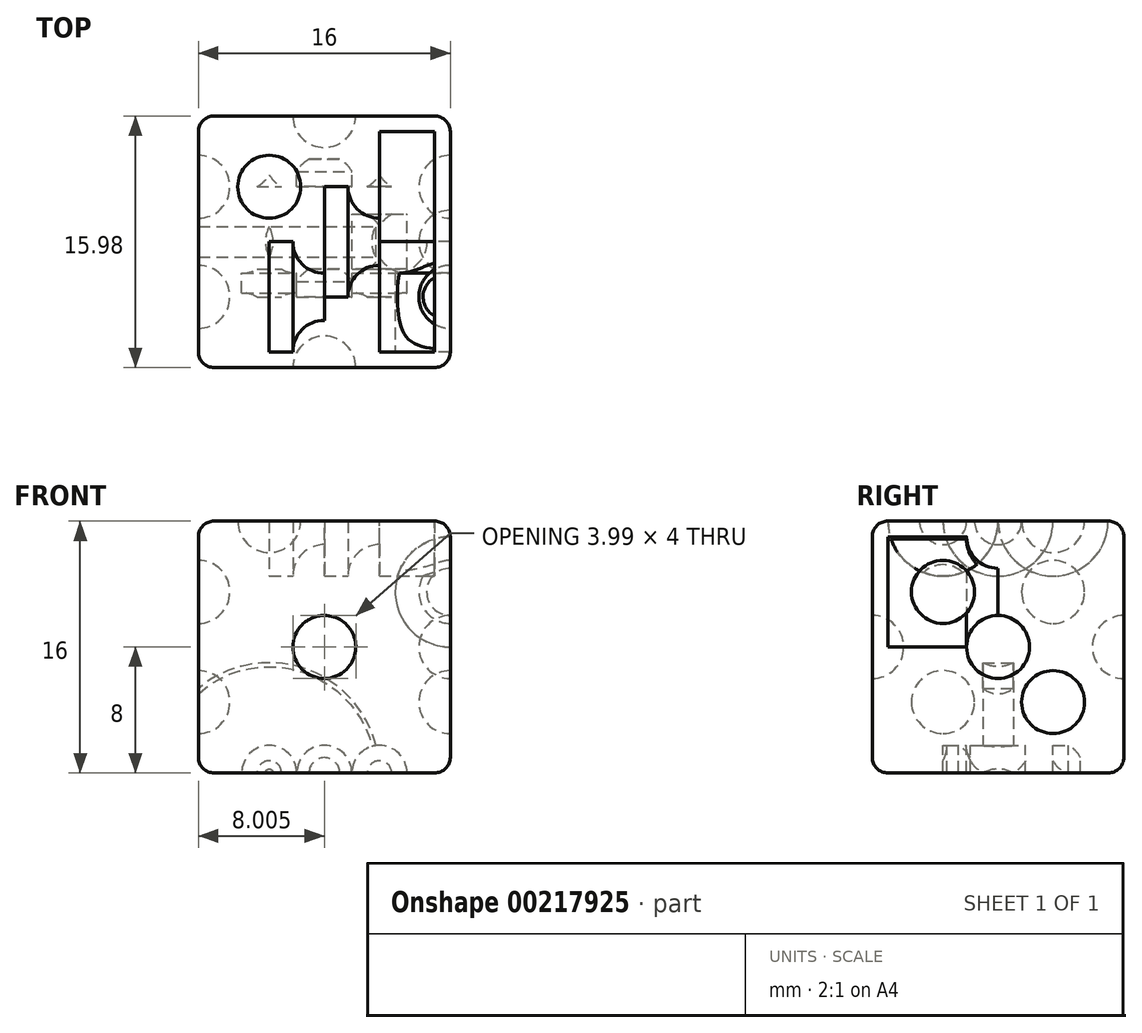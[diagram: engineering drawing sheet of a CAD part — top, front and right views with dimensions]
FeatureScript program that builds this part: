
annotation { "Feature Type Name" : "Feature", "Feature Type Description" : "" }
export const myFeature = defineFeature(function(context is Context, id is Id, definition is map)
    precondition{}
    {
        {
            assignVariable(context, id + "F0", {"name" : "SIZE", "anyValue" : 16});
        }
        {
            var Q0;
            Q0=qCreatedBy(makeId("Top.planeOp"),FACE);
            var sketch = newSketch(context, id + "F1", { "sketchPlane" : qUnion([Q0])});
            skLineSegment(sketch, "E0.bottom", {"start": v(0, 0) * mm, "end": v(16, 0) * mm});
            skLineSegment(sketch, "E0.top", {"start": v(0, -15.98) * mm, "end": v(16, -15.98) * mm});
            skLineSegment(sketch, "E0.left", {"start": v(0, 0) * mm, "end": v(0, -15.98) * mm});
            skLineSegment(sketch, "E0.right", {"start": v(16, 0) * mm, "end": v(16, -15.98) * mm});
            skSolve(sketch);
        }
        {
            var Q0;
            Q0=makeQuery(id+"F1.imprint","IMPRINT",FACE,{"disambiguationData":[TD([[makeQuery(id+"F1.imprint","IMPRINT",EDGE,{"derivedFrom":sQuery(id+"F1.wireOp",EDGE,"E0.bottom")}),-1.0]])]});
            extrude(context, id + "F2", {"entities" : qUnion([Q0]), "depth" : getVariable(context, 'SIZE') * mm});
        }
        {
            var Q0;
            Q0=makeQuery(id+"F2.opExtrude","CAP_EDGE",EDGE,{"disambiguationData":[OSD([sQuery(id+"F1.wireOp",EDGE,"E0.left")])],"isStart":false});
            var Q1;
            Q1=makeQuery(id+"F2.opExtrude","CAP_EDGE",EDGE,{"disambiguationData":[OSD([sQuery(id+"F1.wireOp",EDGE,"E0.top")])],"isStart":false});
            var Q2;
            Q2=makeQuery(id+"F2.opExtrude","CAP_EDGE",EDGE,{"disambiguationData":[OSD([sQuery(id+"F1.wireOp",EDGE,"E0.right")])],"isStart":false});
            var Q3;
            Q3=makeQuery(id+"F2.opExtrude","CAP_EDGE",EDGE,{"disambiguationData":[OSD([sQuery(id+"F1.wireOp",EDGE,"E0.bottom")])],"isStart":false});
            var Q4;
            Q4=makeQuery(id+"F2.opExtrude","SWEPT_EDGE",EDGE,{"disambiguationData":[OSD([sQuery(id+"F1.wireOp",EDGE,"E0.top"),sQuery(id+"F1.wireOp",EDGE,"E0.left")])]});
            var Q5;
            Q5=makeQuery(id+"F2.opExtrude","SWEPT_EDGE",EDGE,{"disambiguationData":[OSD([sQuery(id+"F1.wireOp",EDGE,"E0.bottom"),sQuery(id+"F1.wireOp",EDGE,"E0.left")])]});
            var Q6;
            Q6=makeQuery(id+"F2.opExtrude","SWEPT_EDGE",EDGE,{"disambiguationData":[OSD([sQuery(id+"F1.wireOp",EDGE,"E0.top"),sQuery(id+"F1.wireOp",EDGE,"E0.right")])]});
            var Q7;
            Q7=makeQuery(id+"F2.opExtrude","SWEPT_EDGE",EDGE,{"disambiguationData":[OSD([sQuery(id+"F1.wireOp",EDGE,"E0.bottom"),sQuery(id+"F1.wireOp",EDGE,"E0.right")])]});
            var Q8;
            Q8=makeQuery(id+"F2.opExtrude","CAP_EDGE",EDGE,{"disambiguationData":[OSD([sQuery(id+"F1.wireOp",EDGE,"E0.bottom")])],"isStart":true});
            var Q9;
            Q9=makeQuery(id+"F2.opExtrude","CAP_EDGE",EDGE,{"disambiguationData":[OSD([sQuery(id+"F1.wireOp",EDGE,"E0.left")])],"isStart":true});
            var Q10;
            Q10=makeQuery(id+"F2.opExtrude","CAP_EDGE",EDGE,{"disambiguationData":[OSD([sQuery(id+"F1.wireOp",EDGE,"E0.top")])],"isStart":true});
            var Q11;
            Q11=makeQuery(id+"F2.opExtrude","CAP_EDGE",EDGE,{"disambiguationData":[OSD([sQuery(id+"F1.wireOp",EDGE,"E0.right")])],"isStart":true});
            fillet(context, id + "F3", {"entities" : qUnion([Q0, Q1, Q2, Q3, Q4, Q5, Q6, Q7, Q8, Q9, Q10, Q11]), "radius" : 1 * mm, "tangentPropagation" : true, "allowEdgeOverflow" : false});
        }
        {
            var Q0;
            Q0=makeQuery(id+"F2.opExtrude","SWEPT_FACE",FACE,{"disambiguationData":[OSD([sQuery(id+"F1.wireOp",EDGE,"E0.top")])]});
            var sketch = newSketch(context, id + "F4", { "sketchPlane" : qUnion([Q0])});
            skCircle(sketch, "E1", {"center": v(8, 8) * mm, "radius": 2 * mm});
            skLineSegment(sketch, "E2", {"start": v(1, 15) * mm, "end": v(15, 1) * mm});
            skSolve(sketch);
        }
        {
            var Q0;
            {var subQ0=sQuery(id+"F4.wireOp",EDGE,"E2");var subQ1=sQuery(id+"F4.wireOp",EDGE,"E1");var subQ2=makeQuery(id+"F4.imprint","INTERSECT",VERTEX,{"disambiguationData":[OD(0.0)],"derivedFrom":[subQ1,subQ0]});Q0=makeQuery(id+"F4.imprint","IMPRINT",FACE,{"disambiguationData":[TD([[makeQuery(id+"F4.imprint","IMPRINT",EDGE,{"disambiguationData":[TD([[subQ2,1.0]])],"derivedFrom":subQ1}),1.0]])]});}
            var Q1;
            Q1=sQuery(id+"F4.wireOp",EDGE,"E1");
            var Q2;
            Q2=sQuery(id+"F4.wireOp",EDGE,"E2");
            revolve(context, id + "F5", {"operationType" : NewBodyOperationType.REMOVE, "entities" : qUnion([Q0]), "surfaceEntities" : qUnion([Q1]), "axis" : qUnion([Q2]), "revolveType" : RevolveType.FULL, "oppositeDirection" : true});
        }
        {
            var Q0;
            Q0=makeQuery(id+"F2.opExtrude","SWEPT_FACE",FACE,{"disambiguationData":[OSD([sQuery(id+"F1.wireOp",EDGE,"E0.bottom")])]});
            var sketch = newSketch(context, id + "F6", { "sketchPlane" : qUnion([Q0])});
            skLineSegment(sketch, "E3", {"start": v(-15, 15) * mm, "end": v(-1, 1) * mm});
            skCircle(sketch, "E4", {"center": v(-8, 8) * mm, "radius": 2 * mm});
            skSolve(sketch);
        }
        {
            var Q0;
            {var subQ0=sQuery(id+"F6.wireOp",EDGE,"E4");var subQ1=sQuery(id+"F6.wireOp",EDGE,"E3");var subQ2=makeQuery(id+"F6.imprint","INTERSECT",VERTEX,{"disambiguationData":[OD(0.0)],"derivedFrom":[subQ1,subQ0]});Q0=makeQuery(id+"F6.imprint","IMPRINT",FACE,{"disambiguationData":[TD([[makeQuery(id+"F6.imprint","IMPRINT",EDGE,{"disambiguationData":[TD([[subQ2,-1.0]])],"derivedFrom":subQ1}),1.0]])]});}
            var Q1;
            Q1=sQuery(id+"F6.wireOp",EDGE,"E3");
            revolve(context, id + "F7", {"operationType" : NewBodyOperationType.REMOVE, "entities" : qUnion([Q0]), "axis" : qUnion([Q1]), "revolveType" : RevolveType.FULL});
        }
        {
            var Q0;
            Q0=makeQuery(id+"F2.opExtrude","SWEPT_FACE",FACE,{"disambiguationData":[OSD([sQuery(id+"F1.wireOp",EDGE,"E0.left")])]});
            var sketch = newSketch(context, id + "F8", { "sketchPlane" : qUnion([Q0])});
            skCircle(sketch, "E5", {"center": v(4.5, 11.5) * mm, "radius": 2 * mm});
            skCircle(sketch, "E6", {"center": v(11.49, 4.5) * mm, "radius": 2 * mm});
            skLineSegment(sketch, "E7", {"start": v(8, 15) * mm, "end": v(8, 1) * mm});
            skLineSegment(sketch, "E8", {"start": v(1, 15) * mm, "end": v(1, 1) * mm});
            skLineSegment(sketch, "E9", {"start": v(1, 1) * mm, "end": v(8, 1) * mm});
            skLineSegment(sketch, "E10", {"start": v(1, 15) * mm, "end": v(8, 15) * mm});
            skLineSegment(sketch, "E11", {"start": v(4.5, 15) * mm, "end": v(4.5, 1) * mm});
            skLineSegment(sketch, "E12", {"start": v(8, 15) * mm, "end": v(14.98, 15) * mm});
            skLineSegment(sketch, "E13", {"start": v(14.98, 15) * mm, "end": v(14.98, 1) * mm});
            skLineSegment(sketch, "E14", {"start": v(14.98, 1) * mm, "end": v(8, 1) * mm});
            skLineSegment(sketch, "E15", {"start": v(11.49, 15) * mm, "end": v(11.49, 1) * mm});
            skLineSegment(sketch, "E16", {"start": v(1, 8) * mm, "end": v(14.98, 8) * mm});
            skLineSegment(sketch, "E17", {"start": v(1, 8) * mm, "end": v(1, 15) * mm});
            skLineSegment(sketch, "E18", {"start": v(1, 8) * mm, "end": v(1, 1) * mm});
            skLineSegment(sketch, "E19", {"start": v(14.98, 15) * mm, "end": v(14.98, 8) * mm});
            skLineSegment(sketch, "E20", {"start": v(14.98, 8) * mm, "end": v(14.98, 1) * mm});
            skLineSegment(sketch, "E21", {"start": v(1, 11.5) * mm, "end": v(14.98, 11.5) * mm});
            skLineSegment(sketch, "E22", {"start": v(1, 4.5) * mm, "end": v(14.98, 4.5) * mm});
            skSolve(sketch);
        }
        {
            var Q0;
            {var subQ0=sQuery(id+"F8.wireOp",EDGE,"E11");var subQ1=sQuery(id+"F8.wireOp",EDGE,"E5");var subQ2=makeQuery(id+"F8.imprint","INTERSECT",VERTEX,{"disambiguationData":[OD(0.0)],"derivedFrom":[subQ1,subQ0]});Q0=makeQuery(id+"F8.imprint","IMPRINT",FACE,{"disambiguationData":[TD([[makeQuery(id+"F8.imprint","IMPRINT",EDGE,{"disambiguationData":[TD([[subQ2,-1.0]])],"derivedFrom":subQ1}),1.0]])]});}
            var Q1;
            {var subQ0=sQuery(id+"F8.wireOp",EDGE,"E11");var subQ1=sQuery(id+"F8.wireOp",EDGE,"E5");var subQ2=makeQuery(id+"F8.imprint","INTERSECT",VERTEX,{"disambiguationData":[OD(0.0)],"derivedFrom":[subQ1,subQ0]});Q1=makeQuery(id+"F8.imprint","IMPRINT",FACE,{"disambiguationData":[TD([[makeQuery(id+"F8.imprint","IMPRINT",EDGE,{"disambiguationData":[TD([[subQ2,1.0]])],"derivedFrom":subQ1}),1.0]])]});}
            var Q2;
            Q2=sQuery(id+"F8.wireOp",EDGE,"E21");
            revolve(context, id + "F9", {"operationType" : NewBodyOperationType.REMOVE, "entities" : qUnion([Q0, Q1]), "axis" : qUnion([Q2]), "revolveType" : RevolveType.FULL, "oppositeDirection" : true});
        }
        {
            var Q0;
            {var subQ0=sQuery(id+"F8.wireOp",EDGE,"E22");var subQ1=sQuery(id+"F8.wireOp",EDGE,"E6");var subQ2=makeQuery(id+"F8.imprint","INTERSECT",VERTEX,{"disambiguationData":[OD(1.0)],"derivedFrom":[subQ1,subQ0]});Q0=makeQuery(id+"F8.imprint","IMPRINT",FACE,{"disambiguationData":[TD([[makeQuery(id+"F8.imprint","IMPRINT",EDGE,{"disambiguationData":[TD([[subQ2,-1.0]])],"derivedFrom":subQ1}),1.0]])]});}
            var Q1;
            {var subQ0=sQuery(id+"F8.wireOp",EDGE,"E22");var subQ1=sQuery(id+"F8.wireOp",EDGE,"E6");var subQ2=makeQuery(id+"F8.imprint","INTERSECT",VERTEX,{"disambiguationData":[OD(0.0)],"derivedFrom":[subQ1,subQ0]});Q1=makeQuery(id+"F8.imprint","IMPRINT",FACE,{"disambiguationData":[TD([[makeQuery(id+"F8.imprint","IMPRINT",EDGE,{"disambiguationData":[TD([[subQ2,1.0]])],"derivedFrom":subQ1}),1.0]])]});}
            var Q2;
            Q2=sQuery(id+"F8.wireOp",EDGE,"E22");
            revolve(context, id + "F10", {"operationType" : NewBodyOperationType.REMOVE, "entities" : qUnion([Q0, Q1]), "axis" : qUnion([Q2]), "revolveType" : RevolveType.FULL, "oppositeDirection" : true});
        }
        {
            var Q0;
            Q0=makeQuery(id+"F2.opExtrude","SWEPT_FACE",FACE,{"disambiguationData":[OSD([sQuery(id+"F1.wireOp",EDGE,"E0.right")])]});
            var sketch = newSketch(context, id + "F11", { "sketchPlane" : qUnion([Q0])});
            skLineSegment(sketch, "E23", {"start": v(-8, 15) * mm, "end": v(-8, 1) * mm});
            skLineSegment(sketch, "E24", {"start": v(-8, 1) * mm, "end": v(-14.98, 1) * mm});
            skLineSegment(sketch, "E25", {"start": v(-14.98, 1) * mm, "end": v(-14.98, 15) * mm});
            skLineSegment(sketch, "E26", {"start": v(-14.98, 15) * mm, "end": v(-8, 15) * mm});
            skLineSegment(sketch, "E27", {"start": v(-1, 15) * mm, "end": v(-1, 8) * mm});
            skLineSegment(sketch, "E28", {"start": v(-1, 8) * mm, "end": v(-1, 1) * mm});
            skLineSegment(sketch, "E29", {"start": v(-1, 1) * mm, "end": v(-8, 1) * mm});
            skLineSegment(sketch, "E30", {"start": v(-8, 8) * mm, "end": v(-14.98, 8) * mm});
            skLineSegment(sketch, "E31", {"start": v(-8, 8) * mm, "end": v(-1, 8) * mm});
            skLineSegment(sketch, "E32", {"start": v(-1, 15) * mm, "end": v(-8, 15) * mm});
            skLineSegment(sketch, "E33", {"start": v(-4.5, 15) * mm, "end": v(-4.5, 8) * mm});
            skLineSegment(sketch, "E34", {"start": v(-4.5, 8) * mm, "end": v(-4.5, 1) * mm});
            skLineSegment(sketch, "E35", {"start": v(-11.49, 15) * mm, "end": v(-11.49, 8) * mm});
            skLineSegment(sketch, "E36", {"start": v(-11.49, 8) * mm, "end": v(-11.49, 1) * mm});
            skLineSegment(sketch, "E37", {"start": v(-14.98, 8) * mm, "end": v(-14.98, 15) * mm});
            skLineSegment(sketch, "E38", {"start": v(-1, 11.5) * mm, "end": v(-14.98, 11.5) * mm});
            skLineSegment(sketch, "E39", {"start": v(-14.98, 8) * mm, "end": v(-14.98, 1) * mm});
            skLineSegment(sketch, "E40", {"start": v(-14.98, 4.5) * mm, "end": v(-1, 4.5) * mm});
            skCircle(sketch, "E41", {"center": v(-11.49, 11.5) * mm, "radius": 2 * mm});
            skCircle(sketch, "E42", {"center": v(-8, 8) * mm, "radius": 2 * mm});
            skCircle(sketch, "E43", {"center": v(-4.5, 4.5) * mm, "radius": 2 * mm});
            skSolve(sketch);
        }
        {
            var Q0;
            {var subQ0=sQuery(id+"F11.wireOp",EDGE,"E41");var subQ1=sQuery(id+"F11.wireOp",EDGE,"E35");var subQ2=makeQuery(id+"F11.imprint","INTERSECT",VERTEX,{"disambiguationData":[OD(0.0)],"derivedFrom":[subQ1,subQ0]});Q0=makeQuery(id+"F11.imprint","IMPRINT",FACE,{"disambiguationData":[TD([[makeQuery(id+"F11.imprint","IMPRINT",EDGE,{"disambiguationData":[TD([[subQ2,-1.0]])],"derivedFrom":subQ1}),-1.0]])]});}
            var Q1;
            {var subQ0=sQuery(id+"F11.wireOp",EDGE,"E41");var subQ1=sQuery(id+"F11.wireOp",EDGE,"E35");var subQ2=makeQuery(id+"F11.imprint","INTERSECT",VERTEX,{"disambiguationData":[OD(0.0)],"derivedFrom":[subQ1,subQ0]});Q1=makeQuery(id+"F11.imprint","IMPRINT",FACE,{"disambiguationData":[TD([[makeQuery(id+"F11.imprint","IMPRINT",EDGE,{"disambiguationData":[TD([[subQ2,-1.0]])],"derivedFrom":subQ1}),1.0]])]});}
            var Q2;
            Q2=sQuery(id+"F11.wireOp",EDGE,"E38");
            revolve(context, id + "F12", {"operationType" : NewBodyOperationType.REMOVE, "entities" : qUnion([Q0, Q1]), "axis" : qUnion([Q2]), "revolveType" : RevolveType.FULL, "oppositeDirection" : true});
        }
        {
            var Q0;
            {var subQ1=sQuery(id+"F11.wireOp",EDGE,"E23");var subQ3=sQuery(id+"F11.wireOp",EDGE,"E42");var subQ4=makeQuery(id+"F11.imprint","INTERSECT",VERTEX,{"disambiguationData":[OD(0.0)],"derivedFrom":[subQ1,subQ3]});Q0=makeQuery(id+"F11.imprint","IMPRINT",FACE,{"disambiguationData":[TD([[makeQuery(id+"F11.imprint","IMPRINT",EDGE,{"disambiguationData":[TD([[subQ4,-1.0]])],"derivedFrom":subQ3}),1.0]])]});}
            var Q1;
            {var subQ1=sQuery(id+"F11.wireOp",EDGE,"E23");var subQ3=sQuery(id+"F11.wireOp",EDGE,"E42");var subQ4=makeQuery(id+"F11.imprint","INTERSECT",VERTEX,{"disambiguationData":[OD(0.0)],"derivedFrom":[subQ1,subQ3]});Q1=makeQuery(id+"F11.imprint","IMPRINT",FACE,{"disambiguationData":[TD([[makeQuery(id+"F11.imprint","IMPRINT",EDGE,{"disambiguationData":[TD([[subQ4,1.0]])],"derivedFrom":subQ3}),1.0]])]});}
            var Q2;
            Q2=sQuery(id+"F11.wireOp",EDGE,"E31");
            revolve(context, id + "F13", {"operationType" : NewBodyOperationType.REMOVE, "entities" : qUnion([Q0, Q1]), "axis" : qUnion([Q2]), "revolveType" : RevolveType.FULL, "oppositeDirection" : true});
        }
        {
            var Q0;
            {var subQ0=sQuery(id+"F11.wireOp",EDGE,"E43");var subQ1=sQuery(id+"F11.wireOp",EDGE,"E34");var subQ2=makeQuery(id+"F11.imprint","INTERSECT",VERTEX,{"disambiguationData":[OD(0.0)],"derivedFrom":[subQ1,subQ0]});Q0=makeQuery(id+"F11.imprint","IMPRINT",FACE,{"disambiguationData":[TD([[makeQuery(id+"F11.imprint","IMPRINT",EDGE,{"disambiguationData":[TD([[subQ2,-1.0]])],"derivedFrom":subQ1}),-1.0]])]});}
            var Q1;
            {var subQ0=sQuery(id+"F11.wireOp",EDGE,"E43");var subQ1=sQuery(id+"F11.wireOp",EDGE,"E34");var subQ2=makeQuery(id+"F11.imprint","INTERSECT",VERTEX,{"disambiguationData":[OD(0.0)],"derivedFrom":[subQ1,subQ0]});Q1=makeQuery(id+"F11.imprint","IMPRINT",FACE,{"disambiguationData":[TD([[makeQuery(id+"F11.imprint","IMPRINT",EDGE,{"disambiguationData":[TD([[subQ2,-1.0]])],"derivedFrom":subQ1}),1.0]])]});}
            var Q2;
            Q2=sQuery(id+"F11.wireOp",EDGE,"E40");
            revolve(context, id + "F14", {"operationType" : NewBodyOperationType.REMOVE, "entities" : qUnion([Q0, Q1]), "axis" : qUnion([Q2]), "revolveType" : RevolveType.FULL});
        }
        {
            var Q0;
            Q0=makeQuery(id+"F2.opExtrude","CAP_FACE",FACE,{"disambiguationData":[OSD([sQuery(id+"F1.wireOp",EDGE,"E0.bottom"),sQuery(id+"F1.wireOp",EDGE,"E0.top"),sQuery(id+"F1.wireOp",EDGE,"E0.left"),sQuery(id+"F1.wireOp",EDGE,"E0.right")])],"isStart":false});
            var sketch = newSketch(context, id + "F15", { "sketchPlane" : qUnion([Q0])});
            skLineSegment(sketch, "E44", {"start": v(1, -14.98) * mm, "end": v(1, -1) * mm});
            skLineSegment(sketch, "E45", {"start": v(1, -1) * mm, "end": v(15, -1) * mm});
            skLineSegment(sketch, "E46", {"start": v(15, -1) * mm, "end": v(15, -14.98) * mm});
            skLineSegment(sketch, "E47", {"start": v(15, -14.98) * mm, "end": v(1, -14.98) * mm});
            skLineSegment(sketch, "E48", {"start": v(1, -8) * mm, "end": v(15, -8) * mm});
            skLineSegment(sketch, "E49", {"start": v(8, -1) * mm, "end": v(8, -14.98) * mm});
            skLineSegment(sketch, "E50", {"start": v(1, -14.98) * mm, "end": v(8, -14.98) * mm});
            skLineSegment(sketch, "E51", {"start": v(8, -14.98) * mm, "end": v(15, -14.98) * mm});
            skLineSegment(sketch, "E52", {"start": v(15, -14.98) * mm, "end": v(15, -8) * mm});
            skLineSegment(sketch, "E53", {"start": v(15, -8) * mm, "end": v(15, -1) * mm});
            skLineSegment(sketch, "E54", {"start": v(15, -1) * mm, "end": v(8, -1) * mm});
            skLineSegment(sketch, "E55", {"start": v(8, -1) * mm, "end": v(1, -1) * mm});
            skLineSegment(sketch, "E56", {"start": v(1, -1) * mm, "end": v(1, -8) * mm});
            skLineSegment(sketch, "E57", {"start": v(1, -8) * mm, "end": v(1, -14.98) * mm});
            skLineSegment(sketch, "E58", {"start": v(1, -11.49) * mm, "end": v(15, -11.49) * mm});
            skLineSegment(sketch, "E59", {"start": v(1, -4.5) * mm, "end": v(15, -4.5) * mm});
            skLineSegment(sketch, "E60", {"start": v(4.5, -1) * mm, "end": v(4.5, -14.98) * mm});
            skLineSegment(sketch, "E61", {"start": v(11.5, -1) * mm, "end": v(11.5, -14.98) * mm});
            skCircle(sketch, "E62", {"center": v(4.5, -4.5) * mm, "radius": 2 * mm});
            skCircle(sketch, "E63", {"center": v(4.5, -11.49) * mm, "radius": 2 * mm});
            skCircle(sketch, "E64", {"center": v(11.5, -11.49) * mm, "radius": 2 * mm});
            skCircle(sketch, "E65", {"center": v(11.5, -4.5) * mm, "radius": 2 * mm});
            skCircle(sketch, "E66", {"center": v(8, -8) * mm, "radius": 2 * mm});
            skSolve(sketch);
        }
        {
            var Q0;
            {var subQ0=sQuery(id+"F15.wireOp",EDGE,"E62");var subQ1=sQuery(id+"F15.wireOp",EDGE,"E59");var subQ2=makeQuery(id+"F15.imprint","INTERSECT",VERTEX,{"disambiguationData":[OD(0.0)],"derivedFrom":[subQ1,subQ0]});Q0=makeQuery(id+"F15.imprint","IMPRINT",FACE,{"disambiguationData":[TD([[makeQuery(id+"F15.imprint","IMPRINT",EDGE,{"disambiguationData":[TD([[subQ2,-1.0]])],"derivedFrom":subQ1}),1.0]])]});}
            var Q1;
            {var subQ0=sQuery(id+"F15.wireOp",EDGE,"E60");var subQ1=sQuery(id+"F15.wireOp",EDGE,"E59");var subQ2=makeQuery(id+"F15.imprint","INTERSECT",VERTEX,{"derivedFrom":[subQ1,subQ0]});Q1=makeQuery(id+"F15.imprint","IMPRINT",FACE,{"disambiguationData":[TD([[makeQuery(id+"F15.imprint","IMPRINT",EDGE,{"disambiguationData":[TD([[subQ2,-1.0]])],"derivedFrom":subQ1}),1.0]])]});}
            var Q2;
            {var subQ0=sQuery(id+"F15.wireOp",EDGE,"E65");var subQ1=sQuery(id+"F15.wireOp",EDGE,"E59");var subQ2=makeQuery(id+"F15.imprint","INTERSECT",VERTEX,{"disambiguationData":[OD(0.0)],"derivedFrom":[subQ1,subQ0]});Q2=makeQuery(id+"F15.imprint","IMPRINT",FACE,{"disambiguationData":[TD([[makeQuery(id+"F15.imprint","IMPRINT",EDGE,{"disambiguationData":[TD([[subQ2,-1.0]])],"derivedFrom":subQ1}),1.0]])]});}
            var Q3;
            {var subQ0=sQuery(id+"F15.wireOp",EDGE,"E61");var subQ1=sQuery(id+"F15.wireOp",EDGE,"E59");var subQ2=makeQuery(id+"F15.imprint","INTERSECT",VERTEX,{"derivedFrom":[subQ1,subQ0]});Q3=makeQuery(id+"F15.imprint","IMPRINT",FACE,{"disambiguationData":[TD([[makeQuery(id+"F15.imprint","IMPRINT",EDGE,{"disambiguationData":[TD([[subQ2,-1.0]])],"derivedFrom":subQ1}),1.0]])]});}
            var Q4;
            Q4=sQuery(id+"F15.wireOp",EDGE,"E59");
            revolve(context, id + "F16", {"operationType" : NewBodyOperationType.REMOVE, "entities" : qUnion([Q0, Q1, Q2, Q3]), "axis" : qUnion([Q4]), "revolveType" : RevolveType.FULL, "oppositeDirection" : true});
        }
        {
            var Q0;
            {var subQ0=sQuery(id+"F15.wireOp",EDGE,"E63");var subQ1=sQuery(id+"F15.wireOp",EDGE,"E58");var subQ2=makeQuery(id+"F15.imprint","INTERSECT",VERTEX,{"disambiguationData":[OD(0.0)],"derivedFrom":[subQ1,subQ0]});Q0=makeQuery(id+"F15.imprint","IMPRINT",FACE,{"disambiguationData":[TD([[makeQuery(id+"F15.imprint","IMPRINT",EDGE,{"disambiguationData":[TD([[subQ2,-1.0]])],"derivedFrom":subQ1}),1.0]])]});}
            var Q1;
            {var subQ0=sQuery(id+"F15.wireOp",EDGE,"E60");var subQ1=sQuery(id+"F15.wireOp",EDGE,"E58");var subQ2=makeQuery(id+"F15.imprint","INTERSECT",VERTEX,{"derivedFrom":[subQ1,subQ0]});Q1=makeQuery(id+"F15.imprint","IMPRINT",FACE,{"disambiguationData":[TD([[makeQuery(id+"F15.imprint","IMPRINT",EDGE,{"disambiguationData":[TD([[subQ2,-1.0]])],"derivedFrom":subQ1}),1.0]])]});}
            var Q2;
            {var subQ0=sQuery(id+"F15.wireOp",EDGE,"E64");var subQ1=sQuery(id+"F15.wireOp",EDGE,"E58");var subQ2=makeQuery(id+"F15.imprint","INTERSECT",VERTEX,{"disambiguationData":[OD(0.0)],"derivedFrom":[subQ1,subQ0]});Q2=makeQuery(id+"F15.imprint","IMPRINT",FACE,{"disambiguationData":[TD([[makeQuery(id+"F15.imprint","IMPRINT",EDGE,{"disambiguationData":[TD([[subQ2,-1.0]])],"derivedFrom":subQ1}),1.0]])]});}
            var Q3;
            {var subQ0=sQuery(id+"F15.wireOp",EDGE,"E61");var subQ1=sQuery(id+"F15.wireOp",EDGE,"E58");var subQ2=makeQuery(id+"F15.imprint","INTERSECT",VERTEX,{"derivedFrom":[subQ1,subQ0]});Q3=makeQuery(id+"F15.imprint","IMPRINT",FACE,{"disambiguationData":[TD([[makeQuery(id+"F15.imprint","IMPRINT",EDGE,{"disambiguationData":[TD([[subQ2,-1.0]])],"derivedFrom":subQ1}),1.0]])]});}
            var Q4;
            Q4=sQuery(id+"F15.wireOp",EDGE,"E58");
            revolve(context, id + "F17", {"operationType" : NewBodyOperationType.REMOVE, "entities" : qUnion([Q0, Q1, Q2, Q3]), "axis" : qUnion([Q4]), "revolveType" : RevolveType.FULL, "oppositeDirection" : true});
        }
        {
            var Q0;
            {var subQ0=sQuery(id+"F15.wireOp",EDGE,"E66");var subQ1=sQuery(id+"F15.wireOp",EDGE,"E48");var subQ2=makeQuery(id+"F15.imprint","INTERSECT",VERTEX,{"disambiguationData":[OD(0.0)],"derivedFrom":[subQ1,subQ0]});Q0=makeQuery(id+"F15.imprint","IMPRINT",FACE,{"disambiguationData":[TD([[makeQuery(id+"F15.imprint","IMPRINT",EDGE,{"disambiguationData":[TD([[subQ2,-1.0]])],"derivedFrom":subQ1}),1.0]])]});}
            var Q1;
            {var subQ0=sQuery(id+"F15.wireOp",EDGE,"E49");var subQ1=sQuery(id+"F15.wireOp",EDGE,"E48");var subQ2=makeQuery(id+"F15.imprint","INTERSECT",VERTEX,{"derivedFrom":[subQ1,subQ0]});Q1=makeQuery(id+"F15.imprint","IMPRINT",FACE,{"disambiguationData":[TD([[makeQuery(id+"F15.imprint","IMPRINT",EDGE,{"disambiguationData":[TD([[subQ2,-1.0]])],"derivedFrom":subQ1}),1.0]])]});}
            var Q2;
            Q2=sQuery(id+"F15.wireOp",EDGE,"E48");
            revolve(context, id + "F18", {"operationType" : NewBodyOperationType.REMOVE, "entities" : qUnion([Q0, Q1]), "axis" : qUnion([Q2]), "revolveType" : RevolveType.FULL, "oppositeDirection" : true});
        }
        {
            var Q0;
            Q0=makeQuery(id+"F2.opExtrude","CAP_FACE",FACE,{"disambiguationData":[OSD([sQuery(id+"F1.wireOp",EDGE,"E0.bottom"),sQuery(id+"F1.wireOp",EDGE,"E0.top"),sQuery(id+"F1.wireOp",EDGE,"E0.left"),sQuery(id+"F1.wireOp",EDGE,"E0.right")])],"isStart":true});
            var sketch = newSketch(context, id + "F19", { "sketchPlane" : qUnion([Q0])});
            skLineSegment(sketch, "E67", {"start": v(1, 14.98) * mm, "end": v(1, 1) * mm});
            skLineSegment(sketch, "E68", {"start": v(1, 1) * mm, "end": v(15, 1) * mm});
            skLineSegment(sketch, "E69", {"start": v(15, 1) * mm, "end": v(15, 14.98) * mm});
            skLineSegment(sketch, "E70", {"start": v(15, 14.98) * mm, "end": v(1, 14.98) * mm});
            skLineSegment(sketch, "E71", {"start": v(8, 14.98) * mm, "end": v(8, 1) * mm});
            skLineSegment(sketch, "E72", {"start": v(1, 8) * mm, "end": v(15, 8) * mm});
            skLineSegment(sketch, "E73", {"start": v(1, 14.98) * mm, "end": v(1, 8) * mm});
            skLineSegment(sketch, "E74", {"start": v(1, 1) * mm, "end": v(8, 1) * mm});
            skLineSegment(sketch, "E75", {"start": v(1, 8) * mm, "end": v(1, 1) * mm});
            skLineSegment(sketch, "E76", {"start": v(8, 1) * mm, "end": v(15, 1) * mm});
            skLineSegment(sketch, "E77", {"start": v(15, 1) * mm, "end": v(15, 8) * mm});
            skLineSegment(sketch, "E78", {"start": v(15, 8) * mm, "end": v(15, 14.98) * mm});
            skLineSegment(sketch, "E79", {"start": v(15, 14.98) * mm, "end": v(8, 14.98) * mm});
            skLineSegment(sketch, "E80", {"start": v(8, 14.98) * mm, "end": v(1, 14.98) * mm});
            skLineSegment(sketch, "E81", {"start": v(4.5, 14.98) * mm, "end": v(4.5, 1) * mm});
            skLineSegment(sketch, "E82", {"start": v(11.5, 14.98) * mm, "end": v(11.5, 1) * mm});
            skLineSegment(sketch, "E83", {"start": v(1, 11.49) * mm, "end": v(15, 11.49) * mm});
            skLineSegment(sketch, "E84", {"start": v(1, 4.5) * mm, "end": v(15, 4.5) * mm});
            skLineSegment(sketch, "E85", {"start": v(1, 11.49) * mm, "end": v(1, 8) * mm});
            skLineSegment(sketch, "E86", {"start": v(1, 8) * mm, "end": v(1, 4.5) * mm});
            skLineSegment(sketch, "E87", {"start": v(15, 11.49) * mm, "end": v(15, 8) * mm});
            skLineSegment(sketch, "E88", {"start": v(15, 8) * mm, "end": v(15, 4.5) * mm});
            skLineSegment(sketch, "E89", {"start": v(15, 6.24) * mm, "end": v(1, 6.24) * mm});
            skLineSegment(sketch, "E90", {"start": v(1, 9.74) * mm, "end": v(15, 9.74) * mm});
            skLineSegment(sketch, "E91", {"start": v(1, 14.98) * mm, "end": v(1, 11.49) * mm});
            skLineSegment(sketch, "E92", {"start": v(1, 4.5) * mm, "end": v(1, 1) * mm});
            skLineSegment(sketch, "E93", {"start": v(1, 1) * mm, "end": v(4.5, 1) * mm});
            skLineSegment(sketch, "E94", {"start": v(11.5, 1) * mm, "end": v(15, 1) * mm});
            skLineSegment(sketch, "E95", {"start": v(15, 1) * mm, "end": v(15, 4.5) * mm});
            skLineSegment(sketch, "E96", {"start": v(15, 11.49) * mm, "end": v(15, 14.98) * mm});
            skLineSegment(sketch, "E97", {"start": v(15, 14.98) * mm, "end": v(11.5, 14.98) * mm});
            skLineSegment(sketch, "E98", {"start": v(4.5, 14.98) * mm, "end": v(1, 14.98) * mm});
            skLineSegment(sketch, "E99", {"start": v(2.75, 14.98) * mm, "end": v(2.75, 1) * mm});
            skLineSegment(sketch, "E100", {"start": v(1, 2.75) * mm, "end": v(15, 2.75) * mm});
            skLineSegment(sketch, "E101", {"start": v(13.25, 1) * mm, "end": v(13.25, 14.98) * mm});
            skLineSegment(sketch, "E102", {"start": v(15, 13.23) * mm, "end": v(1, 13.23) * mm});
            skCircle(sketch, "E103", {"center": v(2.75, 13.23) * mm, "radius": 2 * mm});
            skCircle(sketch, "E104", {"center": v(2.75, 2.75) * mm, "radius": 2 * mm});
            skCircle(sketch, "E105", {"center": v(13.25, 2.75) * mm, "radius": 2 * mm});
            skCircle(sketch, "E106", {"center": v(13.25, 13.23) * mm, "radius": 2 * mm});
            skCircle(sketch, "E107", {"center": v(13.25, 8) * mm, "radius": 2 * mm});
            skCircle(sketch, "E108", {"center": v(2.75, 8) * mm, "radius": 2 * mm});
            skLineSegment(sketch, "E109", {"start": v(4.5, 14.98) * mm, "end": v(8, 14.98) * mm});
            skLineSegment(sketch, "E110", {"start": v(8, 14.98) * mm, "end": v(11.5, 14.98) * mm});
            skLineSegment(sketch, "E111", {"start": v(4.5, 1) * mm, "end": v(8, 1) * mm});
            skLineSegment(sketch, "E112", {"start": v(8, 1) * mm, "end": v(11.5, 1) * mm});
            skLineSegment(sketch, "E113", {"start": v(6.25, 1) * mm, "end": v(6.25, 14.98) * mm});
            skLineSegment(sketch, "E114", {"start": v(9.75, 14.98) * mm, "end": v(9.75, 1) * mm});
            skCircle(sketch, "E115", {"center": v(8, 11.49) * mm, "radius": 2 * mm});
            skCircle(sketch, "E116", {"center": v(8, 4.5) * mm, "radius": 2 * mm});
            skSolve(sketch);
        }
        {
            var Q0;
            {var subQ0=sQuery(id+"F19.wireOp",EDGE,"vgZvkRVV-q9ZY-NIho-8I0n-5ifFgJk7Okzj");var subQ1=sQuery(id+"F19.wireOp",EDGE,"E81");var subQ2=makeQuery(id+"F19.imprint","INTERSECT",VERTEX,{"disambiguationData":[OD(0.0)],"derivedFrom":[subQ1,subQ0]});Q0=makeQuery(id+"F19.imprint","IMPRINT",FACE,{"disambiguationData":[TD([[makeQuery(id+"F19.imprint","IMPRINT",EDGE,{"disambiguationData":[TD([[subQ2,-1.0]])],"derivedFrom":subQ1}),-1.0]])]});}
            var Q1;
            {var subQ0=sQuery(id+"F19.wireOp",EDGE,"E83");var subQ1=sQuery(id+"F19.wireOp",EDGE,"E81");var subQ2=makeQuery(id+"F19.imprint","INTERSECT",VERTEX,{"derivedFrom":[subQ1,subQ0]});Q1=makeQuery(id+"F19.imprint","IMPRINT",FACE,{"disambiguationData":[TD([[makeQuery(id+"F19.imprint","IMPRINT",EDGE,{"disambiguationData":[TD([[subQ2,-1.0]])],"derivedFrom":subQ1}),-1.0]])]});}
            var Q2;
            {var subQ0=sQuery(id+"F19.wireOp",EDGE,"V4Pe60rf-3qpI-AFTs-0PZn-PrfCsjdKoN2D");var subQ1=sQuery(id+"F19.wireOp",EDGE,"E72");var subQ2=makeQuery(id+"F19.imprint","INTERSECT",VERTEX,{"disambiguationData":[OD(0.0)],"derivedFrom":[subQ1,subQ0]});Q2=makeQuery(id+"F19.imprint","IMPRINT",FACE,{"disambiguationData":[TD([[makeQuery(id+"F19.imprint","IMPRINT",EDGE,{"disambiguationData":[TD([[subQ2,-1.0]])],"derivedFrom":subQ1}),1.0]])]});}
            var Q3;
            {var subQ0=sQuery(id+"F19.wireOp",EDGE,"V4Pe60rf-3qpI-AFTs-0PZn-PrfCsjdKoN2D");var subQ1=sQuery(id+"F19.wireOp",EDGE,"E72");var subQ2=makeQuery(id+"F19.imprint","INTERSECT",VERTEX,{"disambiguationData":[OD(0.0)],"derivedFrom":[subQ1,subQ0]});Q3=makeQuery(id+"F19.imprint","IMPRINT",FACE,{"disambiguationData":[TD([[makeQuery(id+"F19.imprint","IMPRINT",EDGE,{"disambiguationData":[TD([[subQ2,-1.0]])],"derivedFrom":subQ1}),-1.0]])]});}
            var Q4;
            {var subQ0=sQuery(id+"F19.wireOp",EDGE,"l6YJ2v73-wKKz-WuoQ-KXXM-LcJFSZC3vpOn");var subQ1=sQuery(id+"F19.wireOp",EDGE,"E81");var subQ2=makeQuery(id+"F19.imprint","INTERSECT",VERTEX,{"disambiguationData":[OD(0.0)],"derivedFrom":[subQ1,subQ0]});Q4=makeQuery(id+"F19.imprint","IMPRINT",FACE,{"disambiguationData":[TD([[makeQuery(id+"F19.imprint","IMPRINT",EDGE,{"disambiguationData":[TD([[subQ2,-1.0]])],"derivedFrom":subQ1}),-1.0]])]});}
            var Q5;
            {var subQ0=sQuery(id+"F19.wireOp",EDGE,"E84");var subQ1=sQuery(id+"F19.wireOp",EDGE,"E81");var subQ2=makeQuery(id+"F19.imprint","INTERSECT",VERTEX,{"derivedFrom":[subQ1,subQ0]});Q5=makeQuery(id+"F19.imprint","IMPRINT",FACE,{"disambiguationData":[TD([[makeQuery(id+"F19.imprint","IMPRINT",EDGE,{"disambiguationData":[TD([[subQ2,-1.0]])],"derivedFrom":subQ1}),-1.0]])]});}
            var Q6;
            Q6=sQuery(id+"F19.wireOp",EDGE,"E81");
            revolve(context, id + "F20", {"operationType" : NewBodyOperationType.REMOVE, "entities" : qUnion([Q0, Q1, Q2, Q3, Q4, Q5]), "axis" : qUnion([Q6]), "revolveType" : RevolveType.FULL, "oppositeDirection" : true});
        }
        {
            var Q0;
            {var subQ0=sQuery(id+"F19.wireOp",EDGE,"CJIanx8B-APFl-5aag-5BiE-M5nfP2R59bhR");var subQ1=sQuery(id+"F19.wireOp",EDGE,"E82");var subQ2=makeQuery(id+"F19.imprint","INTERSECT",VERTEX,{"disambiguationData":[OD(0.0)],"derivedFrom":[subQ1,subQ0]});Q0=makeQuery(id+"F19.imprint","IMPRINT",FACE,{"disambiguationData":[TD([[makeQuery(id+"F19.imprint","IMPRINT",EDGE,{"disambiguationData":[TD([[subQ2,-1.0]])],"derivedFrom":subQ1}),1.0]])]});}
            var Q1;
            {var subQ0=sQuery(id+"F19.wireOp",EDGE,"E83");var subQ1=sQuery(id+"F19.wireOp",EDGE,"E82");var subQ2=makeQuery(id+"F19.imprint","INTERSECT",VERTEX,{"derivedFrom":[subQ1,subQ0]});Q1=makeQuery(id+"F19.imprint","IMPRINT",FACE,{"disambiguationData":[TD([[makeQuery(id+"F19.imprint","IMPRINT",EDGE,{"disambiguationData":[TD([[subQ2,-1.0]])],"derivedFrom":subQ1}),1.0]])]});}
            var Q2;
            {var subQ0=sQuery(id+"F19.wireOp",EDGE,"E82");var subQ1=sQuery(id+"F19.wireOp",EDGE,"E72");var subQ2=makeQuery(id+"F19.imprint","INTERSECT",VERTEX,{"derivedFrom":[subQ1,subQ0]});Q2=makeQuery(id+"F19.imprint","IMPRINT",FACE,{"disambiguationData":[TD([[makeQuery(id+"F19.imprint","IMPRINT",EDGE,{"disambiguationData":[TD([[subQ2,-1.0]])],"derivedFrom":subQ1}),1.0]])]});}
            var Q3;
            {var subQ0=sQuery(id+"F19.wireOp",EDGE,"E82");var subQ1=sQuery(id+"F19.wireOp",EDGE,"E72");var subQ2=makeQuery(id+"F19.imprint","INTERSECT",VERTEX,{"derivedFrom":[subQ1,subQ0]});Q3=makeQuery(id+"F19.imprint","IMPRINT",FACE,{"disambiguationData":[TD([[makeQuery(id+"F19.imprint","IMPRINT",EDGE,{"disambiguationData":[TD([[subQ2,-1.0]])],"derivedFrom":subQ1}),-1.0]])]});}
            var Q4;
            {var subQ0=sQuery(id+"F19.wireOp",EDGE,"QhomiRVJ-wV6E-Ku5z-LJW5-OjjMtzpaDoxe");var subQ1=sQuery(id+"F19.wireOp",EDGE,"E82");var subQ2=makeQuery(id+"F19.imprint","INTERSECT",VERTEX,{"disambiguationData":[OD(0.0)],"derivedFrom":[subQ1,subQ0]});Q4=makeQuery(id+"F19.imprint","IMPRINT",FACE,{"disambiguationData":[TD([[makeQuery(id+"F19.imprint","IMPRINT",EDGE,{"disambiguationData":[TD([[subQ2,-1.0]])],"derivedFrom":subQ1}),1.0]])]});}
            var Q5;
            {var subQ0=sQuery(id+"F19.wireOp",EDGE,"E84");var subQ1=sQuery(id+"F19.wireOp",EDGE,"E82");var subQ2=makeQuery(id+"F19.imprint","INTERSECT",VERTEX,{"derivedFrom":[subQ1,subQ0]});Q5=makeQuery(id+"F19.imprint","IMPRINT",FACE,{"disambiguationData":[TD([[makeQuery(id+"F19.imprint","IMPRINT",EDGE,{"disambiguationData":[TD([[subQ2,-1.0]])],"derivedFrom":subQ1}),1.0]])]});}
            var Q6;
            Q6=sQuery(id+"F19.wireOp",EDGE,"E82");
            revolve(context, id + "F21", {"operationType" : NewBodyOperationType.REMOVE, "entities" : qUnion([Q0, Q1, Q2, Q3, Q4, Q5]), "axis" : qUnion([Q6]), "revolveType" : RevolveType.FULL, "oppositeDirection" : true});
        }
        {
            var Q0;
            {var subQ0=sQuery(id+"F19.wireOp",EDGE,"QVsbU9qe-qi2V-xHKW-JmVe-DGFGDNWW14si");var subQ1=sQuery(id+"F19.wireOp",EDGE,"E71");var subQ2=makeQuery(id+"F19.imprint","INTERSECT",VERTEX,{"disambiguationData":[OD(0.0)],"derivedFrom":[subQ1,subQ0]});Q0=makeQuery(id+"F19.imprint","IMPRINT",FACE,{"disambiguationData":[TD([[makeQuery(id+"F19.imprint","IMPRINT",EDGE,{"disambiguationData":[TD([[subQ2,-1.0]])],"derivedFrom":subQ1}),1.0]])]});}
            var Q1;
            {var subQ0=sQuery(id+"F19.wireOp",EDGE,"8KEjiZfs-LIBH-2Its-EPA5-eHQxQN4lQsyr");var subQ1=sQuery(id+"F19.wireOp",EDGE,"E71");var subQ2=makeQuery(id+"F19.imprint","INTERSECT",VERTEX,{"disambiguationData":[OD(0.0)],"derivedFrom":[subQ1,subQ0]});Q1=makeQuery(id+"F19.imprint","IMPRINT",FACE,{"disambiguationData":[TD([[makeQuery(id+"F19.imprint","IMPRINT",EDGE,{"disambiguationData":[TD([[subQ2,-1.0]])],"derivedFrom":subQ1}),1.0]])]});}
            var Q2;
            {var subQ0=sQuery(id+"F19.wireOp",EDGE,"E84");var subQ1=sQuery(id+"F19.wireOp",EDGE,"E71");var subQ2=makeQuery(id+"F19.imprint","INTERSECT",VERTEX,{"derivedFrom":[subQ1,subQ0]});Q2=makeQuery(id+"F19.imprint","IMPRINT",FACE,{"disambiguationData":[TD([[makeQuery(id+"F19.imprint","IMPRINT",EDGE,{"disambiguationData":[TD([[subQ2,-1.0]])],"derivedFrom":subQ1}),1.0]])]});}
            var Q3;
            {var subQ0=sQuery(id+"F19.wireOp",EDGE,"E83");var subQ1=sQuery(id+"F19.wireOp",EDGE,"E71");var subQ2=makeQuery(id+"F19.imprint","INTERSECT",VERTEX,{"derivedFrom":[subQ1,subQ0]});Q3=makeQuery(id+"F19.imprint","IMPRINT",FACE,{"disambiguationData":[TD([[makeQuery(id+"F19.imprint","IMPRINT",EDGE,{"disambiguationData":[TD([[subQ2,-1.0]])],"derivedFrom":subQ1}),1.0]])]});}
            var Q4;
            Q4=sQuery(id+"F19.wireOp",EDGE,"E71");
            revolve(context, id + "F22", {"operationType" : NewBodyOperationType.REMOVE, "entities" : qUnion([Q0, Q1, Q2, Q3]), "axis" : qUnion([Q4]), "revolveType" : RevolveType.FULL, "oppositeDirection" : true});
        }
    });
